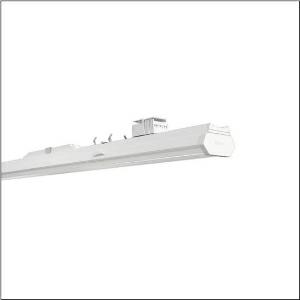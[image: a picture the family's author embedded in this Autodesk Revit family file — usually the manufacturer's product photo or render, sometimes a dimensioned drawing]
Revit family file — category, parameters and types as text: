
# Revit family: licross_r__21_protected_mo_52tp12dn48xg_9fce
name_source: partatom
category: Lighting Fixtures
units: mm (PartAtom-declared; Revit-internal decimal feet)

## family parameters
Cut with Voids When Loaded = No
Host = Face
Light Source = No
Part Type = Normal
Room Calculation Point = No
Round Connector Dimension = Use Diameter
Shared = No

## types (1)
- --- (1 x LED, 8000 lm, 45.3 W, 4000K)
    Apparent Load = 45 VA
    CIE Flux Codes = 73 92 98 99 100
    Color Rendering = 80
    Color Temperature = 4000K
    Default Elevation = 1800 mm
    Description = Licross® 21 Protected MO, luminaire insert, of sheet steel, galvanised, coil coated, white, length: 1.500mm, width: 90mm, height: 103mm, LED rated luminous flux: 8.000lm, light colour: 840, control gear: DALI 2, with plug, 5-pole, with phase selection, mains connection: 220..240V, AC, 50/60Hz, rated input power: 45W, halogen-free wiring, primary light control with lens, of plastic, primary optical cover: cover, of PMMA, light emission: direct distribution, primary light characteristic: symmetric, protection rating (complete): IP64, insulation class (complete): insulation class I (protective earthing), certification: CE, ENEC, VDE, UKCA, protection symbol: D if used in an environment with conductive dust loads with corresponding accessories, impact resistance: IK06, permissible ambient temperature for indoor applications: -25..+45°C, corresponds to IFS (International Featured Standards) requirements for safety and quality in the food industry, reducing of maximum allowable ambient temperature of 5°C with ceiling mounting, LABS conformity tested according to VDMA 24364:2018-05, packaging unit: 1 piece
    Height = 92 mm
    Lamp = 1 x LED
    Lamp Light Flux = 8000 lm
    Lamp Power = 45.3 W
    Lamp count = 1
    Length = 1500 mm
    Luminous efficacy = 177 lm/W
    Manufacturer = Siteco
    ModVariant = No
    Model = 52TP12DN48XG
    Mounting Place = Ceiling
    Mounting Type = Pendant
    Number of Poles = 1
    OnlyDefault = Yes
    Power Factor = 1
    Product Name = Licross® 21 Protected MO
    Product group = luminaire insert
    ProductGroupID = 902
    Protection Class = Protection class I
    Protection Degree = IP 64
    RLX_Detail_Level = 1
    RLX_Emergency_Light_Flux = 0 lm
    RLX_Emergency_Type = 0
    RLX_Emergency_Type_DB = No
    RlxData = <blob elided: 24321 chars, md5=893ae2bf>
    Socket = socket
    Standby Power = 0 W
    System Light Flux = 8000 lm
    System Power = 45 W
    Type Comments = factory setting: luminous flux: 100 % | dim-lin: 254 | 305 mA
    Type Image = l_1256148.jpg
    URL = http://relux.com
    VarID = @adj_128636
    Voltage = 0 V
    Weight = 0.00 kg
    Width = 88 mm

## geometry (parser evidence)
native form markers: Blend x4, Sweep x11
no freeform markers — native parametric forms only
